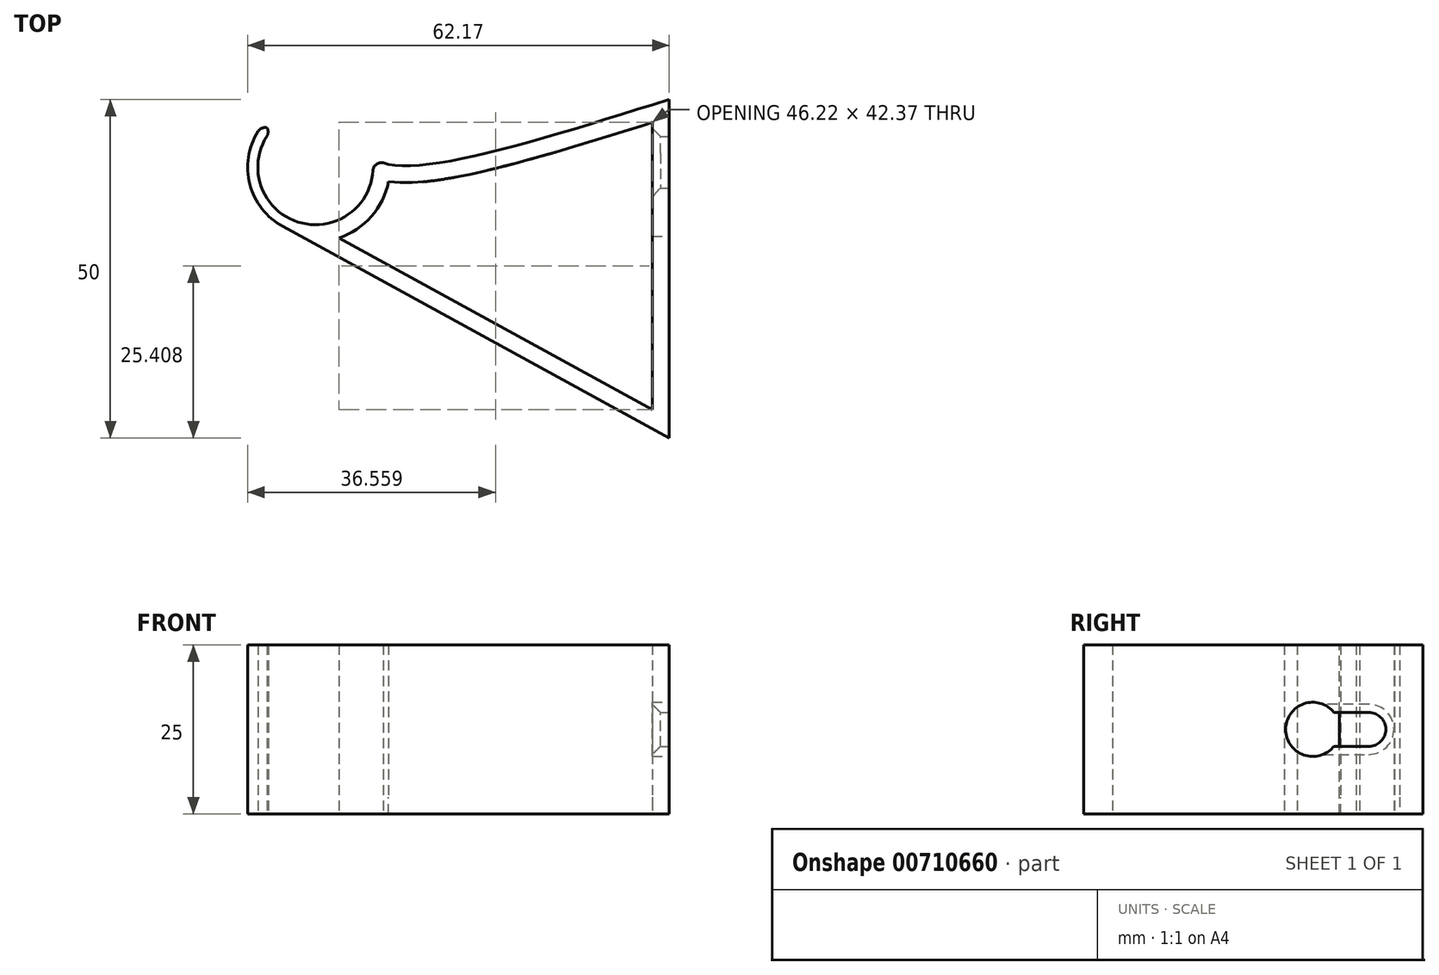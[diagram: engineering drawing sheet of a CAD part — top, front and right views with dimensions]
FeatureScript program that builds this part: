
annotation { "Feature Type Name" : "Feature", "Feature Type Description" : "" }
export const myFeature = defineFeature(function(context is Context, id is Id, definition is map)
    precondition{}
    {
        {
            var Q0;
            Q0=qCreatedBy(makeId("Top.planeOp"),FACE);
            var sketch = newSketch(context, id + "F0", { "sketchPlane" : qUnion([Q0])});
            skLineSegment(sketch, "E0", {"start": v(0, 0) * mm, "end": v(0, 26.02) * mm});
            skLineSegment(sketch, "E1", {"start": v(0, 26.02) * mm, "end": v(0, -23.98) * mm});
            skArc(sketch, "E2", {"start": v(-58.72, 21.44) * mm, "mid": v(-54.79, 7.93) * mm, "end": v(-43.7, 16.59) * mm});
            skArc(sketch, "E3", {"start": v(-59.88, 22.4) * mm, "mid": v(-55.25, 6.5) * mm, "end": v(-42.2, 16.69) * mm});
            skLineSegment(sketch, "E4", {"start": v(0, -23.98) * mm, "end": v(-56.98, 7.25) * mm});
            skLineSegment(sketch, "E5", {"start": v(-43.7, 16.59) * mm, "end": v(-42.2, 16.69) * mm});
            skFitSpline(sketch, "E6", {"points": [v(0, 26.02) * mm, v(-42.2, 16.69) * mm, v(-45.12, 20.77) * mm], "startDerivative": vector(-73.38, -23.16) * mm, "endDerivative": vector(-5.8, 19.67) * mm});
            skLineSegment(sketch, "E7", {"start": v(-58.72, 21.44) * mm, "end": v(-59.88, 22.4) * mm});
            skSolve(sketch);
        }
        {
            var Q0;
            {var subQ2=sQuery(id+"F0.wireOp",EDGE,"E4");Q0=makeQuery(id+"F0.imprint","IMPRINT",FACE,{"disambiguationData":[TD([[makeQuery(id+"F0.imprint","IMPRINT",EDGE,{"derivedFrom":subQ2}),-1.0]])]});}
            var Q1;
            Q1=makeQuery(id+"F0.imprint","IMPRINT",FACE,{"disambiguationData":[TD([[makeQuery(id+"F0.imprint","IMPRINT",EDGE,{"derivedFrom":sQuery(id+"F0.wireOp",EDGE,"E2")}),-1.0]])]});
            extrude(context, id + "F1", {"entities" : qUnion([Q0, Q1]), "depth" : 25 * mm, "offsetDistance" : 25 * mm});
        }
        {
            var Q0;
            Q0=makeQuery(id+"F1.opExtrude","SWEPT_EDGE",EDGE,{"disambiguationData":[OSD([sQuery(id+"F0.wireOp",EDGE,"E2"),sQuery(id+"F0.wireOp",EDGE,"E7")])]});
            var Q1;
            Q1=makeQuery(id+"F1.opExtrude","SWEPT_EDGE",EDGE,{"disambiguationData":[OSD([sQuery(id+"F0.wireOp",EDGE,"E3"),sQuery(id+"F0.wireOp",EDGE,"E7")])]});
            var Q2;
            Q2=makeQuery(id+"F1.opExtrude","SWEPT_EDGE",EDGE,{"disambiguationData":[OSD([sQuery(id+"F0.wireOp",EDGE,"E2"),sQuery(id+"F0.wireOp",EDGE,"E5")])]});
            fillet(context, id + "F2", {"entities" : qUnion([Q0, Q1, Q2]), "radius" : 1.2 * mm, "tangentPropagation" : true, "allowEdgeOverflow" : false});
        }
        {
            var Q0;
            Q0=makeQuery(id+"F1.opExtrude","CAP_FACE",FACE,{"disambiguationData":[OSD([sQuery(id+"F0.wireOp",EDGE,"E1"),sQuery(id+"F0.wireOp",EDGE,"E2"),sQuery(id+"F0.wireOp",EDGE,"E3"),sQuery(id+"F0.wireOp",EDGE,"E4"),sQuery(id+"F0.wireOp",EDGE,"E5"),sQuery(id+"F0.wireOp",EDGE,"E6"),sQuery(id+"F0.wireOp",EDGE,"E7")])],"isStart":false});
            shell(context, id + "F3", {"entities" : qUnion([Q0]), "thickness" : 2.5 * mm});
        }
        {
            var Q0;
            Q0=makeQuery(id+"F3.opShell","OFFSET_FACE",FACE,{"disambiguationData":[OSD([sQuery(id+"F0.wireOp",EDGE,"E1"),sQuery(id+"F0.wireOp",EDGE,"E2"),sQuery(id+"F0.wireOp",EDGE,"E3"),sQuery(id+"F0.wireOp",EDGE,"E4"),sQuery(id+"F0.wireOp",EDGE,"E5"),sQuery(id+"F0.wireOp",EDGE,"E6"),sQuery(id+"F0.wireOp",EDGE,"E7")])]});
            extrude(context, id + "F4", {"entities" : qUnion([Q0]), "operationType" : NewBodyOperationType.REMOVE, "oppositeDirection" : true, "depth" : 25 * mm, "offsetDistance" : 25 * mm});
        }
        {
            var Q0;
            Q0=makeQuery(id+"F1.opExtrude","SWEPT_FACE",FACE,{"disambiguationData":[OSD([sQuery(id+"F0.wireOp",EDGE,"E1")])]});
            var sketch = newSketch(context, id + "F5", { "sketchPlane" : qUnion([Q0])});
            skCircle(sketch, "E8", {"center": v(9.8, 12.5) * mm, "radius": 4 * mm});
            skPoint(sketch, "E8.centerSnap0", {"position": v(26.02, 12.5) * mm});
            skCircle(sketch, "E9", {"center": v(18.06, 12.5) * mm, "radius": 2.5 * mm});
            skLineSegment(sketch, "E10", {"start": v(18.06, 15) * mm, "end": v(12.92, 15) * mm});
            skLineSegment(sketch, "E11", {"start": v(18.06, 10) * mm, "end": v(12.92, 10) * mm});
            skSolve(sketch);
        }
        {
            var Q0;
            {var subQ0=sQuery(id+"F5.wireOp",EDGE,"E8");var subQ1=makeQuery(id+"F5.imprint","INTERSECT",VERTEX,{"derivedFrom":[subQ0,sQuery(id+"F5.wireOp",EDGE,"E10")]});Q0=makeQuery(id+"F5.imprint","IMPRINT",FACE,{"disambiguationData":[TD([[makeQuery(id+"F5.imprint","IMPRINT",EDGE,{"disambiguationData":[TD([[subQ1,-1.0]])],"derivedFrom":subQ0}),1.0]])]});}
            var Q1;
            {var subQ0=sQuery(id+"F5.wireOp",EDGE,"E9");var subQ1=makeQuery(id+"F5.imprint","INTERSECT",VERTEX,{"derivedFrom":[subQ0,sQuery(id+"F5.wireOp",EDGE,"E10")]});Q1=makeQuery(id+"F5.imprint","IMPRINT",FACE,{"disambiguationData":[TD([[makeQuery(id+"F5.imprint","IMPRINT",EDGE,{"disambiguationData":[TD([[subQ1,-1.0]])],"derivedFrom":subQ0}),1.0]])]});}
            var Q2;
            {var subQ0=sQuery(id+"F5.wireOp",EDGE,"E10");Q2=makeQuery(id+"F5.imprint","IMPRINT",FACE,{"disambiguationData":[TD([[makeQuery(id+"F5.imprint","IMPRINT",EDGE,{"derivedFrom":subQ0}),1.0]])]});}
            extrude(context, id + "F6", {"entities" : qUnion([Q0, Q1, Q2]), "operationType" : NewBodyOperationType.REMOVE, "oppositeDirection" : true, "depth" : 3 * mm, "offsetDistance" : 25 * mm});
        }
        {
            var Q0;
            {var subQ0=sQuery(id+"F0.wireOp",EDGE,"E1");Q0=makeQuery(id+"F6.boolean.opBoolean","INTERSECT",EDGE,{"derivedFrom":[makeQuery(id+"F4.boolean.opBoolean","MERGE",FACE,{"derivedFrom":[makeQuery(id+"F3.opShell","OFFSET_FACE",FACE,{"disambiguationData":[OSD([subQ0])]}),makeQuery(id+"F4.opExtrude","SWEPT_FACE",FACE,{"disambiguationData":[OSD([subQ0])]})]}),makeQuery(id+"F6.opExtrude","SWEPT_FACE",FACE,{"disambiguationData":[OSD([sQuery(id+"F5.wireOp",EDGE,"E11")])]})]});}
            var Q1;
            {var subQ0=sQuery(id+"F0.wireOp",EDGE,"E1");Q1=makeQuery(id+"F6.boolean.opBoolean","INTERSECT",EDGE,{"derivedFrom":[makeQuery(id+"F4.boolean.opBoolean","MERGE",FACE,{"derivedFrom":[makeQuery(id+"F3.opShell","OFFSET_FACE",FACE,{"disambiguationData":[OSD([subQ0])]}),makeQuery(id+"F4.opExtrude","SWEPT_FACE",FACE,{"disambiguationData":[OSD([subQ0])]})]}),makeQuery(id+"F6.opExtrude","SWEPT_FACE",FACE,{"disambiguationData":[OSD([sQuery(id+"F5.wireOp",EDGE,"E10")])]})]});}
            var Q2;
            {var subQ0=sQuery(id+"F0.wireOp",EDGE,"E1");Q2=makeQuery(id+"F6.boolean.opBoolean","INTERSECT",EDGE,{"derivedFrom":[makeQuery(id+"F4.boolean.opBoolean","MERGE",FACE,{"derivedFrom":[makeQuery(id+"F3.opShell","OFFSET_FACE",FACE,{"disambiguationData":[OSD([subQ0])]}),makeQuery(id+"F4.opExtrude","SWEPT_FACE",FACE,{"disambiguationData":[OSD([subQ0])]})]}),makeQuery(id+"F6.opExtrude","SWEPT_FACE",FACE,{"disambiguationData":[OSD([sQuery(id+"F5.wireOp",EDGE,"E9")])]})]});}
            chamfer(context, id + "F7", {"entities" : qUnion([Q0, Q1, Q2]), "width" : 1.2 * mm, "tangentPropagation" : true});
        }
    });
